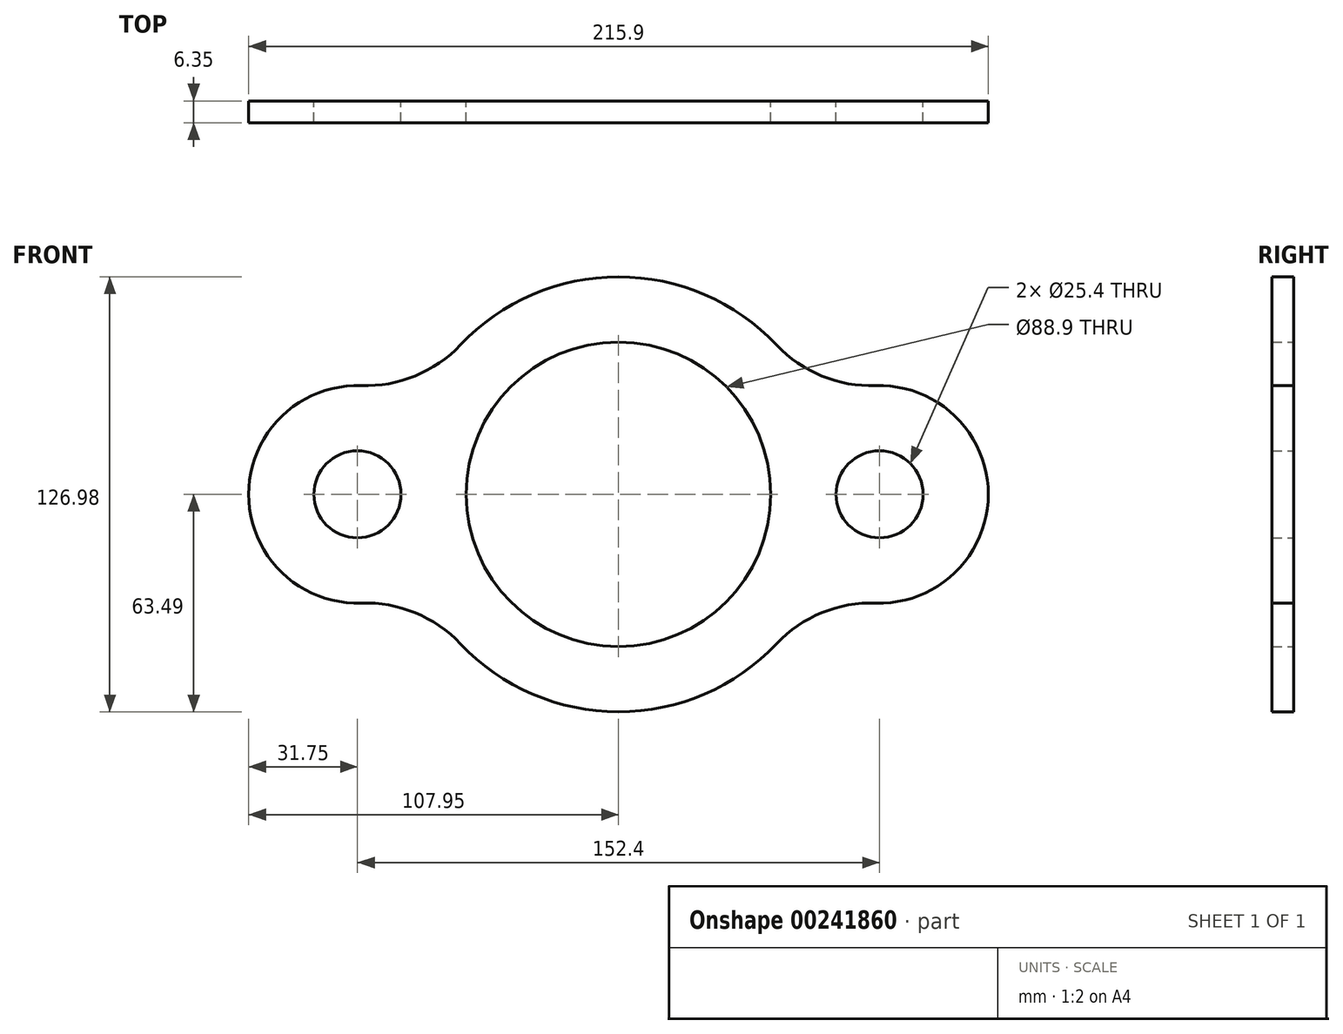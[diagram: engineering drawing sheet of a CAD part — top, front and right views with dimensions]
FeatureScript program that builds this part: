
annotation { "Feature Type Name" : "Feature", "Feature Type Description" : "" }
export const myFeature = defineFeature(function(context is Context, id is Id, definition is map)
    precondition{}
    {
        {
            var Q0;
            Q0=qCreatedBy(makeId("Front.planeOp"),FACE);
            var sketch = newSketch(context, id + "F0", { "sketchPlane" : qUnion([Q0])});
            skArc(sketch, "E0", {"start": v(75.11, -31.73) * mm, "mid": v(107.95, 0) * mm, "end": v(75.11, 31.73) * mm});
            skCircle(sketch, "E1", {"center": v(0, 0) * mm, "radius": 44.45 * mm});
            skArc(sketch, "E2", {"start": v(-46.12, -43.63) * mm, "mid": v(0, -63.49) * mm, "end": v(46.12, -43.63) * mm});
            skArc(sketch, "E3", {"start": v(-75.11, 31.73) * mm, "mid": v(-107.95, 0) * mm, "end": v(-75.11, -31.73) * mm});
            skCircle(sketch, "E4", {"center": v(-76.2, 0) * mm, "radius": 12.7 * mm});
            skCircle(sketch, "E5", {"center": v(76.2, 0) * mm, "radius": 12.7 * mm});
            skArc(sketch, "E6", {"start": v(-75.11, 31.73) * mm, "mid": v(-59.34, 34.56) * mm, "end": v(-46.12, 43.63) * mm});
            skArc(sketch, "E7", {"start": v(46.12, 43.63) * mm, "mid": v(59.34, 34.56) * mm, "end": v(75.11, 31.73) * mm});
            skArc(sketch, "E8.trimOffspring", {"start": v(46.12, 43.63) * mm, "mid": v(0, 63.49) * mm, "end": v(-46.12, 43.63) * mm});
            skArc(sketch, "E9", {"start": v(-46.12, -43.63) * mm, "mid": v(-59.34, -34.56) * mm, "end": v(-75.11, -31.73) * mm});
            skArc(sketch, "E10", {"start": v(75.11, -31.73) * mm, "mid": v(59.34, -34.56) * mm, "end": v(46.12, -43.63) * mm});
            skSolve(sketch);
        }
        {
            var Q0;
            Q0=makeQuery(id+"F0.imprint","IMPRINT",FACE,{"disambiguationData":[TD([[makeQuery(id+"F0.imprint","IMPRINT",EDGE,{"derivedFrom":sQuery(id+"F0.wireOp",EDGE,"E0")}),1.0]])]});
            extrude(context, id + "F1", {"entities" : qUnion([Q0]), "depth" : 6.35 * mm});
        }
    });
